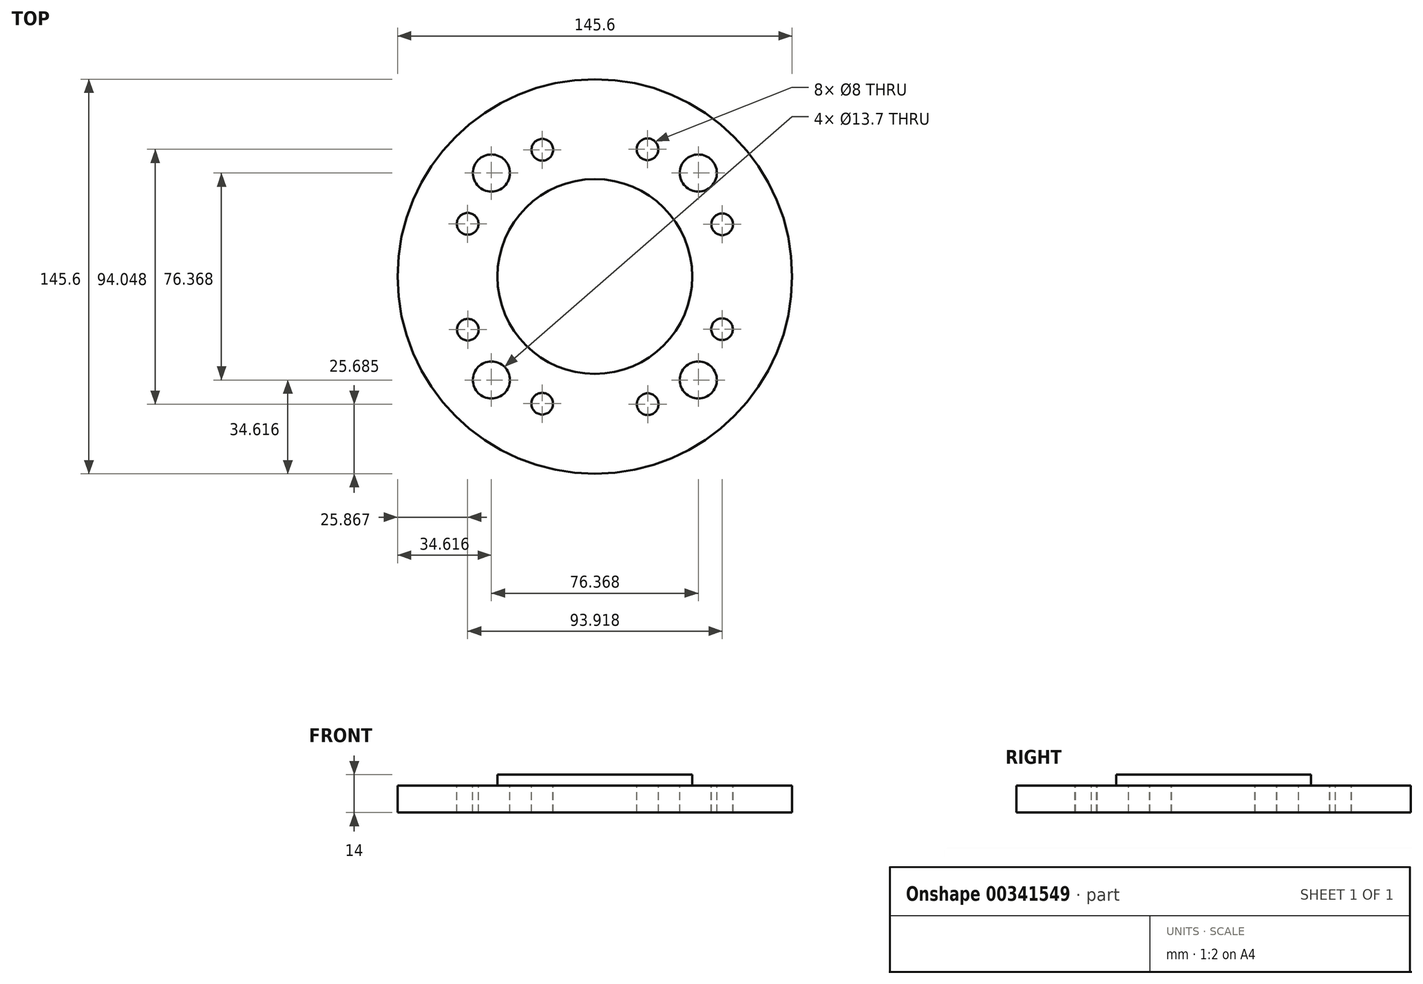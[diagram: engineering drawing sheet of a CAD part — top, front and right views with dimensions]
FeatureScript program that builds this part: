
annotation { "Feature Type Name" : "Feature", "Feature Type Description" : "" }
export const myFeature = defineFeature(function(context is Context, id is Id, definition is map)
    precondition{}
    {
        {
            var Q0;
            Q0=qCreatedBy(makeId("Top.planeOp"),FACE);
            var sketch = newSketch(context, id + "F0", { "sketchPlane" : qUnion([Q0])});
            skCircle(sketch, "E0", {"center": v(0, 0) * mm, "radius": 50.8 * mm, "construction": true});
            skCircle(sketch, "E1", {"center": v(0, 50.8) * mm, "radius": 5.75 * mm, "construction": true});
            skCircle(sketch, "E2.1.0", {"center": v(-50.8, 0) * mm, "radius": 5.75 * mm, "construction": true});
            skCircle(sketch, "E2.2.0", {"center": v(0, -50.8) * mm, "radius": 5.75 * mm, "construction": true});
            skCircle(sketch, "E2.3.0", {"center": v(50.8, 0) * mm, "radius": 5.75 * mm, "construction": true});
            skCircle(sketch, "E3", {"center": v(0, 0) * mm, "radius": 72.8 * mm});
            skCircle(sketch, "E4", {"center": v(0, 0) * mm, "radius": 54 * mm, "construction": true});
            skCircle(sketch, "E5", {"center": v(0, 0) * mm, "radius": 35.95 * mm});
            skCircle(sketch, "E6", {"center": v(19.44, 46.93) * mm, "radius": 4 * mm});
            skCircle(sketch, "E7", {"center": v(46.93, -19.44) * mm, "radius": 4 * mm});
            skCircle(sketch, "E8", {"center": v(-19.44, -46.93) * mm, "radius": 4 * mm});
            skCircle(sketch, "E9", {"center": v(-46.93, 19.44) * mm, "radius": 4 * mm});
            skCircle(sketch, "E10", {"center": v(38.18, -38.18) * mm, "radius": 6.85 * mm});
            skCircle(sketch, "E11", {"center": v(-38.18, 38.18) * mm, "radius": 6.85 * mm});
            skCircle(sketch, "E12", {"center": v(38.18, 38.18) * mm, "radius": 6.85 * mm});
            skCircle(sketch, "E13", {"center": v(-38.18, -38.18) * mm, "radius": 6.85 * mm});
            skCircle(sketch, "E14", {"center": v(46.98, 19.26) * mm, "radius": 4 * mm});
            skCircle(sketch, "E15", {"center": v(19.5, -47.11) * mm, "radius": 4 * mm});
            skCircle(sketch, "E16", {"center": v(-46.88, -19.62) * mm, "radius": 4 * mm});
            skCircle(sketch, "E17", {"center": v(-19.39, 46.75) * mm, "radius": 4 * mm});
            skSolve(sketch);
        }
        {
            var Q0;
            Q0=makeQuery(id+"F0.imprint","IMPRINT",FACE,{"disambiguationData":[TD([[makeQuery(id+"F0.imprint","IMPRINT",EDGE,{"derivedFrom":sQuery(id+"F0.wireOp",EDGE,"E3")}),1.0]])]});
            var Q1;
            Q1=makeQuery(id+"F0.imprint","IMPRINT",FACE,{"disambiguationData":[TD([[makeQuery(id+"F0.imprint","IMPRINT",EDGE,{"derivedFrom":sQuery(id+"F0.wireOp",EDGE,"E5")}),1.0]])]});
            extrude(context, id + "F1", {"entities" : qUnion([Q0, Q1]), "oppositeDirection" : true, "depth" : 10 * mm});
        }
        {
            var Q0;
            Q0=makeQuery(id+"F0.imprint","IMPRINT",FACE,{"disambiguationData":[TD([[makeQuery(id+"F0.imprint","IMPRINT",EDGE,{"derivedFrom":sQuery(id+"F0.wireOp",EDGE,"E5")}),1.0]])]});
            extrude(context, id + "F2", {"entities" : qUnion([Q0]), "operationType" : NewBodyOperationType.ADD, "depth" : 4 * mm});
        }
    });
